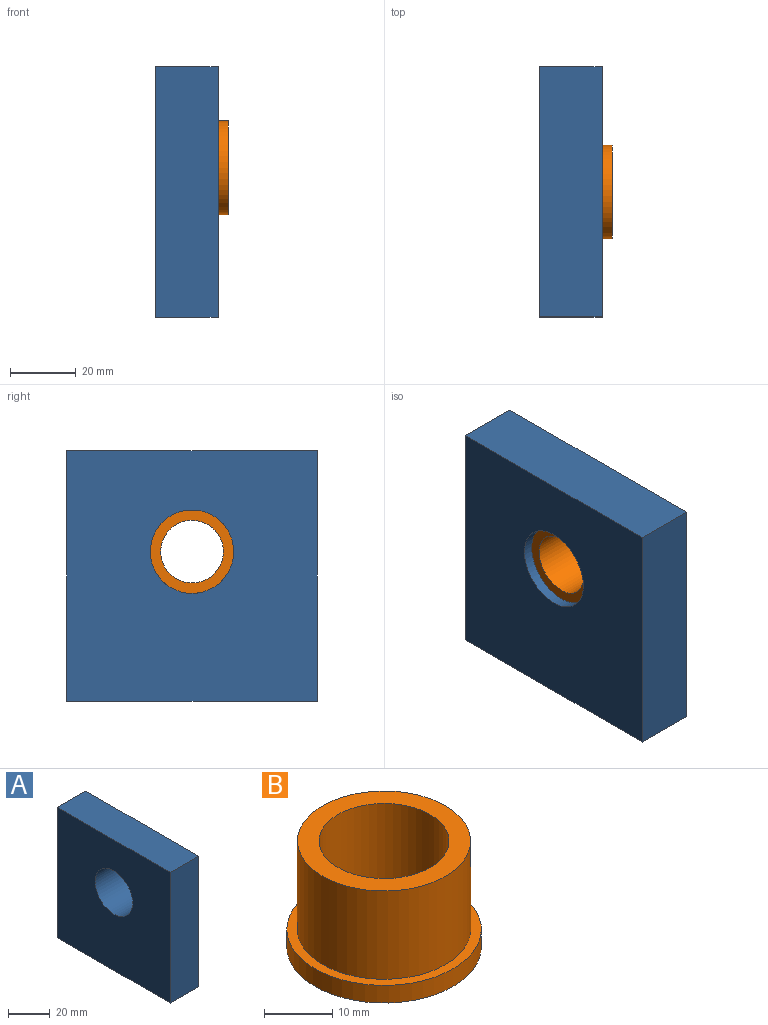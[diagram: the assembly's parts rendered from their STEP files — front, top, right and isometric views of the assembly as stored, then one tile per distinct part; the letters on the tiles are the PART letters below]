
ASSEMBLY  parts=2 mates=1
PART A: 11 faces, bbox 19.1x76.2x76.2 mm
  f0: plane 76.2x19.05mm, normal (0,-1,0), area 1451.6mm2, adj f1,f3,f4,f5
  f1: plane 76.2x19.05mm, normal (0,0,-1), area 1388.3mm2, adj f0,f2,f4,f5,f7,f9
  f2: plane 76.2x19.05mm, normal (0,1,0), area 1451.6mm2, adj f1,f3,f4,f5
  f3: plane 76.2x19.05mm, normal (0,0,1), area 1451.6mm2, adj f0,f2,f4,f5
  f4: plane 76.2x76.2mm, normal (1,0,0), area 5299.7mm2, adj f0,f1,f2,f3,f6
  f5: plane 76.2x76.2mm, normal (-1,0,0), area 5299.7mm2, adj f0,f1,f2,f3,f6
  f6: cylinder r=12.7mm len=25.4mm, axis (1,0,0), area 1520.1mm2, adj f4,f5
  f7: cylinder r=3.17mm len=25.4mm, axis (0,0,-1), area 506.7mm2, adj f1,f8
  f8: plane 6.35x6.35mm, normal (0,0,-1), area 31.7mm2, adj f7
  f9: cylinder r=3.17mm len=25.4mm, axis (0,0,-1), area 506.7mm2, adj f1,f10
  f10: plane 6.35x6.35mm, normal (0,0,-1), area 31.7mm2, adj f9
PART B: 6 faces, bbox 28.6x28.6x19.1 mm
  f0: plane 25.45x25.45mm, normal (0,0,1), area 222.2mm2, adj f2,f3
  f1: plane 28.58x28.58mm, normal (0,0,-1), area 354.8mm2, adj f3,f5
  f2: cylinder r=12.73mm len=25.45mm, axis (0,0,-1), area 1269.3mm2, adj f0,f4
  f3: cylinder r=9.55mm len=19.1mm, axis (0,0,-1), area 1143.1mm2, adj f0,f1
  f4: plane 28.58x28.58mm, normal (0,0,1), area 132.6mm2, adj f2,f5
  f5: cylinder r=14.29mm len=28.58mm, axis (0,0,-1), area 285mm2, adj f1,f4
PLACE A t=(-19.05,0,0)mm
PLACE B rot(axis=(0,-1,0),90deg) t=(3.18,38.1,45.52)mm
MATE fastened B.f2 <-> A.f6  axis (1,0,0) through (0,38.1,45.52)mm
